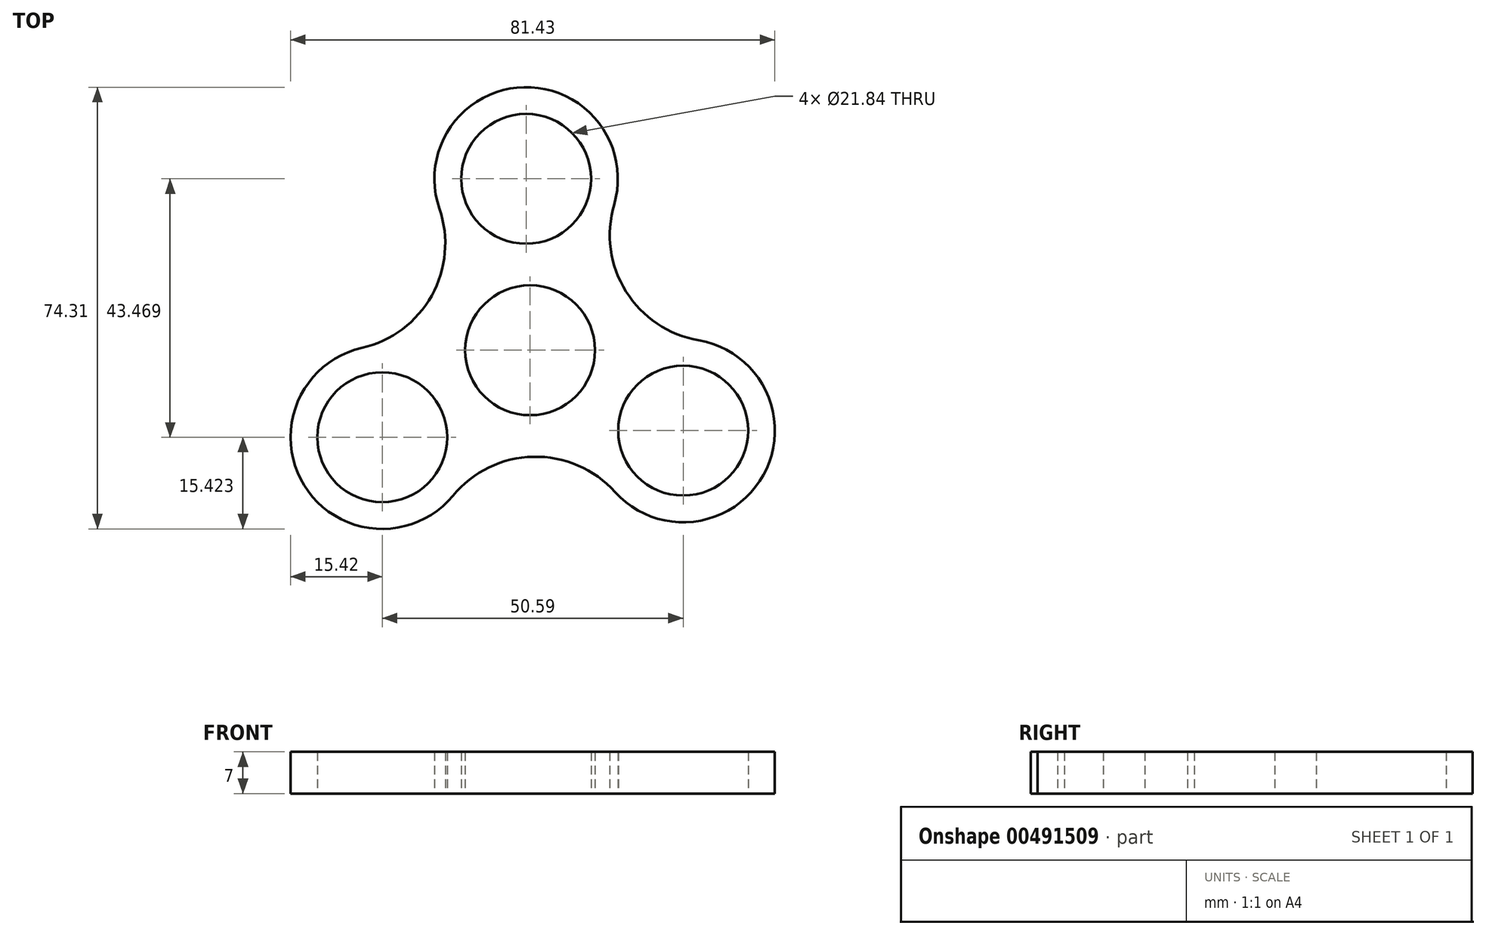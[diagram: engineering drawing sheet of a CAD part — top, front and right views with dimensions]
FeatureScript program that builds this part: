
annotation { "Feature Type Name" : "Feature", "Feature Type Description" : "" }
export const myFeature = defineFeature(function(context is Context, id is Id, definition is map)
    precondition{}
    {
        {
            var Q0;
            Q0=qCreatedBy(makeId("Top.planeOp"),FACE);
            var sketch = newSketch(context, id + "F0", { "sketchPlane" : qUnion([Q0])});
            skCircle(sketch, "E0", {"center": v(0, 0) * mm, "radius": 10.92 * mm});
            skCircle(sketch, "E1", {"center": v(-0.66, 28.83) * mm, "radius": 10.92 * mm});
            skPoint(sketch, "E2.center", {"position": v(0.34, 0.05) * mm});
            skArc(sketch, "E3", {"start": v(14.13, 24.49) * mm, "mid": v(-1.02, 44.25) * mm, "end": v(-15.24, 23.81) * mm});
            skArc(sketch, "E4", {"start": v(-28.27, 0.4) * mm, "mid": v(-37.98, -22.73) * mm, "end": v(-12.96, -24.45) * mm});
            skArc(sketch, "E5", {"start": v(14.3, -23.85) * mm, "mid": v(39.25, -20.96) * mm, "end": v(28.35, 1.68) * mm});
            skArc(sketch, "E6", {"start": v(-28.27, 0.4) * mm, "mid": v(-16.53, 9.2) * mm, "end": v(-15.24, 23.81) * mm});
            skArc(sketch, "E7", {"start": v(14.13, 24.49) * mm, "mid": v(16.13, 9.9) * mm, "end": v(28.35, 1.68) * mm});
            skArc(sketch, "E8", {"start": v(14.3, -23.85) * mm, "mid": v(0.53, -17.91) * mm, "end": v(-12.96, -24.45) * mm});
            skCircle(sketch, "E9", {"center": v(-24.85, -14.64) * mm, "radius": 10.92 * mm});
            skCircle(sketch, "E10", {"center": v(25.74, -13.52) * mm, "radius": 10.92 * mm});
            skSolve(sketch);
        }
        {
            var Q0;
            Q0=makeQuery(id+"F0.imprint","IMPRINT",FACE,{"disambiguationData":[TD([[makeQuery(id+"F0.imprint","IMPRINT",EDGE,{"derivedFrom":sQuery(id+"F0.wireOp",EDGE,"E1")}),-1.0]])]});
            var Q1;
            Q1=makeQuery(id+"F0.imprint","IMPRINT",FACE,{"disambiguationData":[TD([[makeQuery(id+"F0.imprint","IMPRINT",EDGE,{"derivedFrom":sQuery(id+"F0.wireOp",EDGE,"E2.2.0")}),-1.0]])]});
            var Q2;
            Q2=makeQuery(id+"F0.imprint","IMPRINT",FACE,{"disambiguationData":[TD([[makeQuery(id+"F0.imprint","IMPRINT",EDGE,{"derivedFrom":sQuery(id+"F0.wireOp",EDGE,"E2.1.0")}),-1.0]])]});
            var Q3;
            Q3=makeQuery(id+"F0.imprint","IMPRINT",FACE,{"disambiguationData":[TD([[makeQuery(id+"F0.imprint","IMPRINT",EDGE,{"derivedFrom":sQuery(id+"F0.wireOp",EDGE,"4O9khdKf-2qk6-6eEU-YUye-EU3OGTiNBHui")}),-1.0]])]});
            var Q4;
            Q4=makeQuery(id+"F0.imprint","IMPRINT",FACE,{"disambiguationData":[TD([[makeQuery(id+"F0.imprint","IMPRINT",EDGE,{"derivedFrom":sQuery(id+"F0.wireOp",EDGE,"E0")}),-1.0]])]});
            extrude(context, id + "F1", {"entities" : qUnion([Q0, Q1, Q2, Q3, Q4]), "depth" : 7 * mm, "offsetDistance" : 25 * mm});
        }
    });
